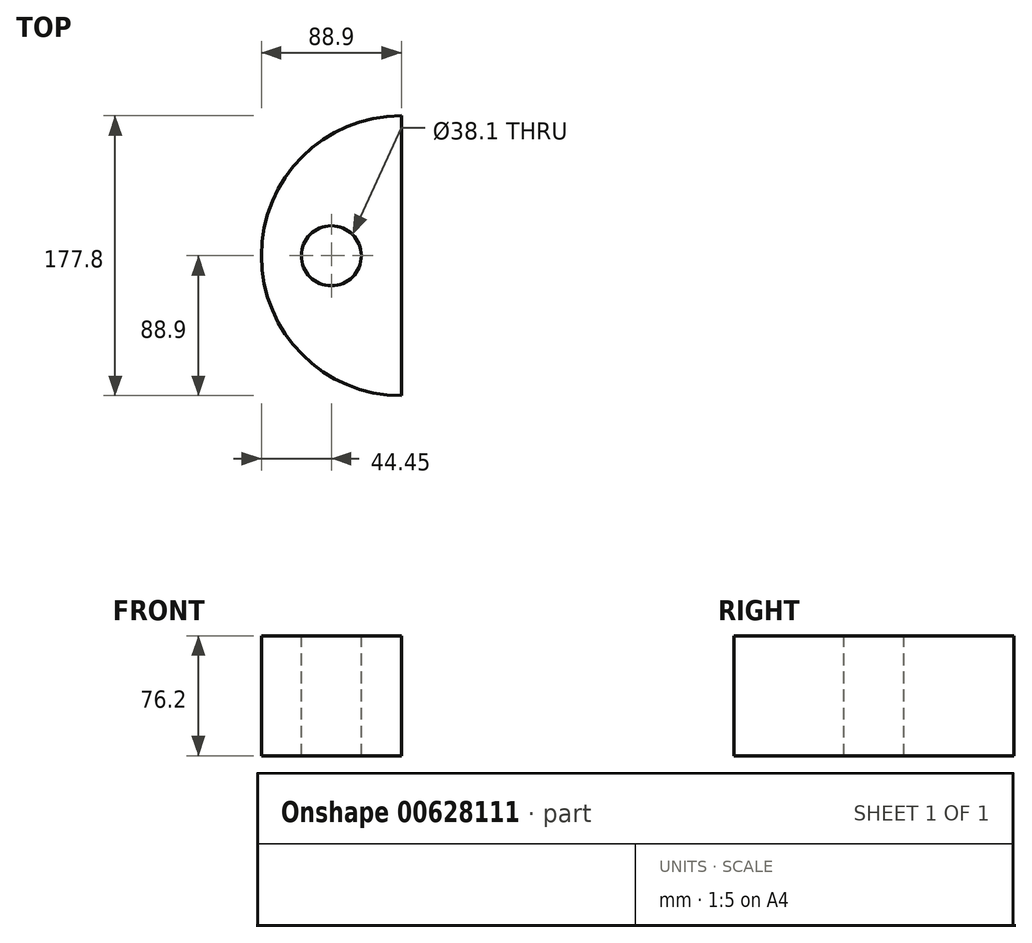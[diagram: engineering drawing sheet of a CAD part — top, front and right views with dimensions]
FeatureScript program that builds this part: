
annotation { "Feature Type Name" : "Feature", "Feature Type Description" : "" }
export const myFeature = defineFeature(function(context is Context, id is Id, definition is map)
    precondition{}
    {
        {
            var Q0;
            Q0=qCreatedBy(makeId("Top.planeOp"),FACE);
            var sketch = newSketch(context, id + "F0", { "sketchPlane" : qUnion([Q0])});
            skArc(sketch, "E0", {"start": v(0, 88.9) * mm, "mid": v(-88.9, 0) * mm, "end": v(0, -88.9) * mm});
            skLineSegment(sketch, "E1", {"start": v(0, 88.9) * mm, "end": v(0, -88.9) * mm});
            skSolve(sketch);
        }
        {
            var Q0;
            Q0=makeQuery(id+"F0.imprint","IMPRINT",FACE,{"disambiguationData":[TD([[makeQuery(id+"F0.imprint","IMPRINT",EDGE,{"derivedFrom":sQuery(id+"F0.wireOp",EDGE,"E0")}),1.0]])]});
            extrude(context, id + "F1", {"entities" : qUnion([Q0]), "depth" : 76.2 * mm, "offsetDistance" : 25.4 * mm});
        }
        {
            var Q0;
            Q0=makeQuery(id+"F1.opExtrude","CAP_FACE",FACE,{"disambiguationData":[OSD([sQuery(id+"F0.wireOp",EDGE,"E0"),sQuery(id+"F0.wireOp",EDGE,"E1")])],"isStart":false});
            var sketch = newSketch(context, id + "F2", { "sketchPlane" : qUnion([Q0])});
            skCircle(sketch, "E2", {"center": v(-44.45, 0) * mm, "radius": 19.05 * mm});
            skSolve(sketch);
        }
        {
            var Q0;
            Q0=makeQuery(id+"F2.imprint","IMPRINT",FACE,{"disambiguationData":[TD([[makeQuery(id+"F2.imprint","IMPRINT",EDGE,{"derivedFrom":sQuery(id+"F2.wireOp",EDGE,"E2")}),1.0]])]});
            extrude(context, id + "F3", {"entities" : qUnion([Q0]), "operationType" : NewBodyOperationType.REMOVE, "oppositeDirection" : true, "depth" : 76.2 * mm, "offsetDistance" : 25.4 * mm});
        }
    });
